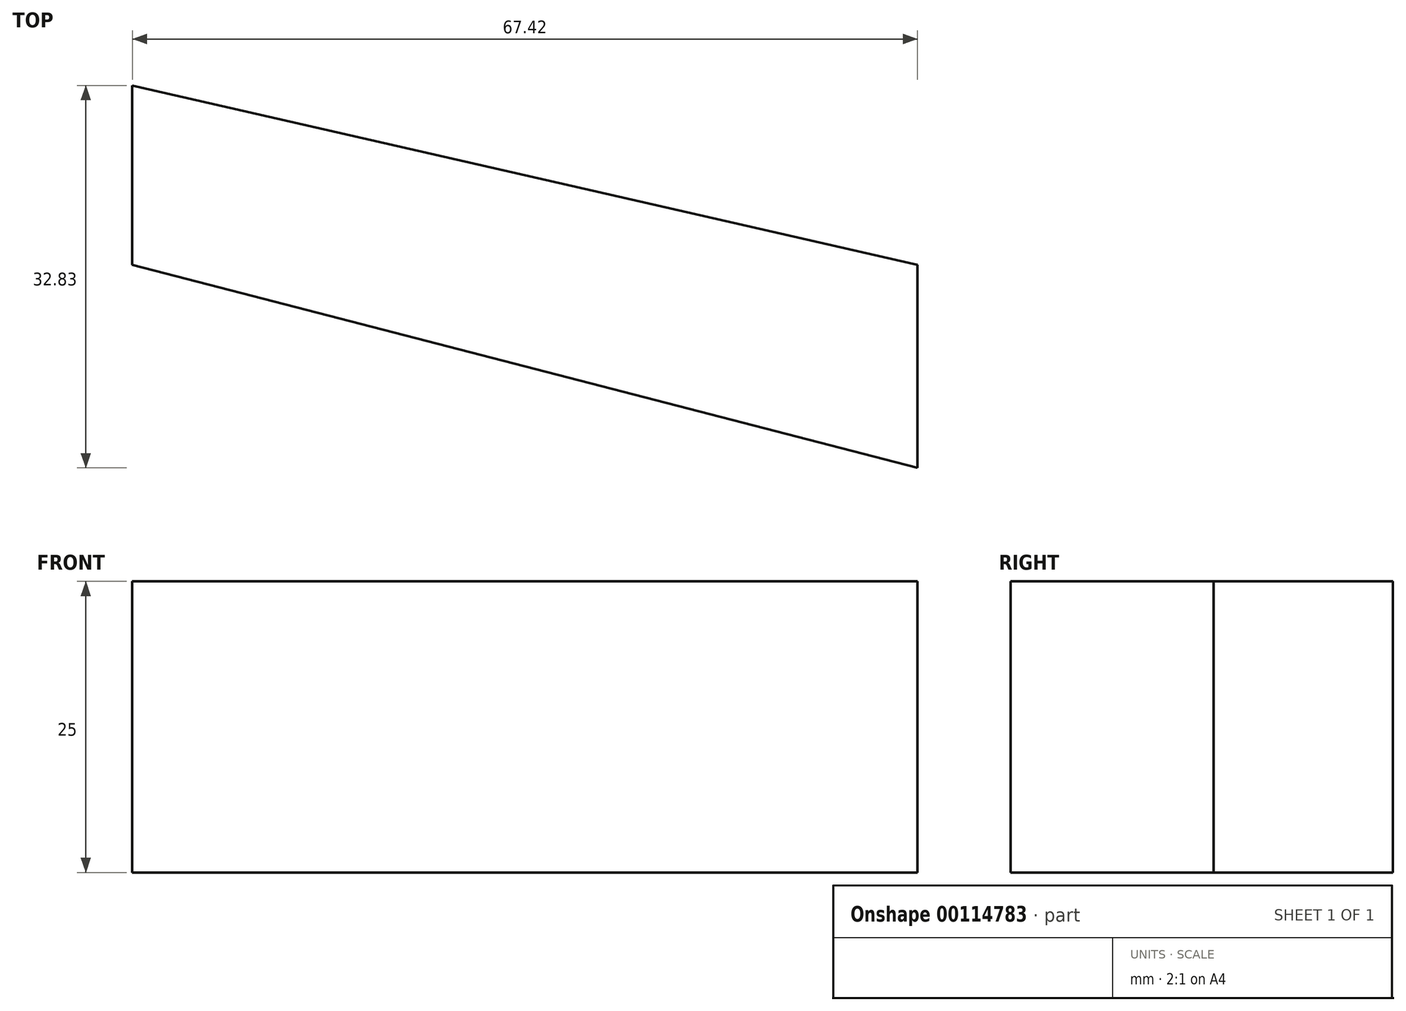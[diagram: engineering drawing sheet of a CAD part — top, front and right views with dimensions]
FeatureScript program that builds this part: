
annotation { "Feature Type Name" : "Feature", "Feature Type Description" : "" }
export const myFeature = defineFeature(function(context is Context, id is Id, definition is map)
    precondition{}
    {
        {
            var Q0;
            Q0=qCreatedBy(makeId("Top.planeOp"),FACE);
            var sketch = newSketch(context, id + "F0", { "sketchPlane" : qUnion([Q0])});
            skLineSegment(sketch, "E0", {"start": v(0, 0) * mm, "end": v(-67.42, 15.4) * mm});
            skLineSegment(sketch, "E1", {"start": v(-67.42, 0) * mm, "end": v(-67.42, 15.4) * mm});
            skLineSegment(sketch, "E2", {"start": v(-67.42, 0) * mm, "end": v(0, -17.44) * mm});
            skLineSegment(sketch, "E3", {"start": v(0, -17.44) * mm, "end": v(0, 0) * mm});
            skSolve(sketch);
        }
        {
            var Q0;
            Q0 = qSketchRegion(id + "F0", true);
            extrude(context, id + "F1", {"entities" : qUnion([Q0]), "oppositeDirection" : true, "depth" : 25 * mm});
        }
    });
